# Revit family: Ленточный двухскатный зенитный фонарь M8CITY_Д_ГЛУХ
name_source: partatom
category: Оборудование
revit_build: Autodesk Revit 2017 (Build: 20170118_1100(x64)
units: mm (PartAtom-declared; Revit-internal decimal feet)

## family parameters
Всегда вертикально = Нет
Общий = Нет
Основа = Крыша
При загрузке вырезать с полостями = Нет
Размер круглого соединителя = Использовать диаметр
Тип детали = Нормальный
Точка расчета площади = Нет

## types (1)
- Зенитный фонарь M8CITY Л-Д-ГЛУХ
    N арок = 2
    N растров = 3
    URL = www.m8city.by
    Высота = 673 мм
    Высота основания = 600 мм
    Длина = 2600 мм
    Длина проёма = 2600 мм
    Длина проёма ввод = 2600 мм
    Изготовитель = ООО Завод М8 Сити Про
    Крайний растр = 815 мм
    Описание = Ленточный зенитный фонарь M8CITY в премиальном исполнении глухой с двускатным сводом
    Угол наклона к горизонту = 30.00°
    Угол наклона к горизонту ном = 30.00°
    Шаг типовой = 1060 мм
    Ширина = 3500 мм
    Ширина проёма = 3500 мм
    Ширина проёма ввод = 3500 мм
